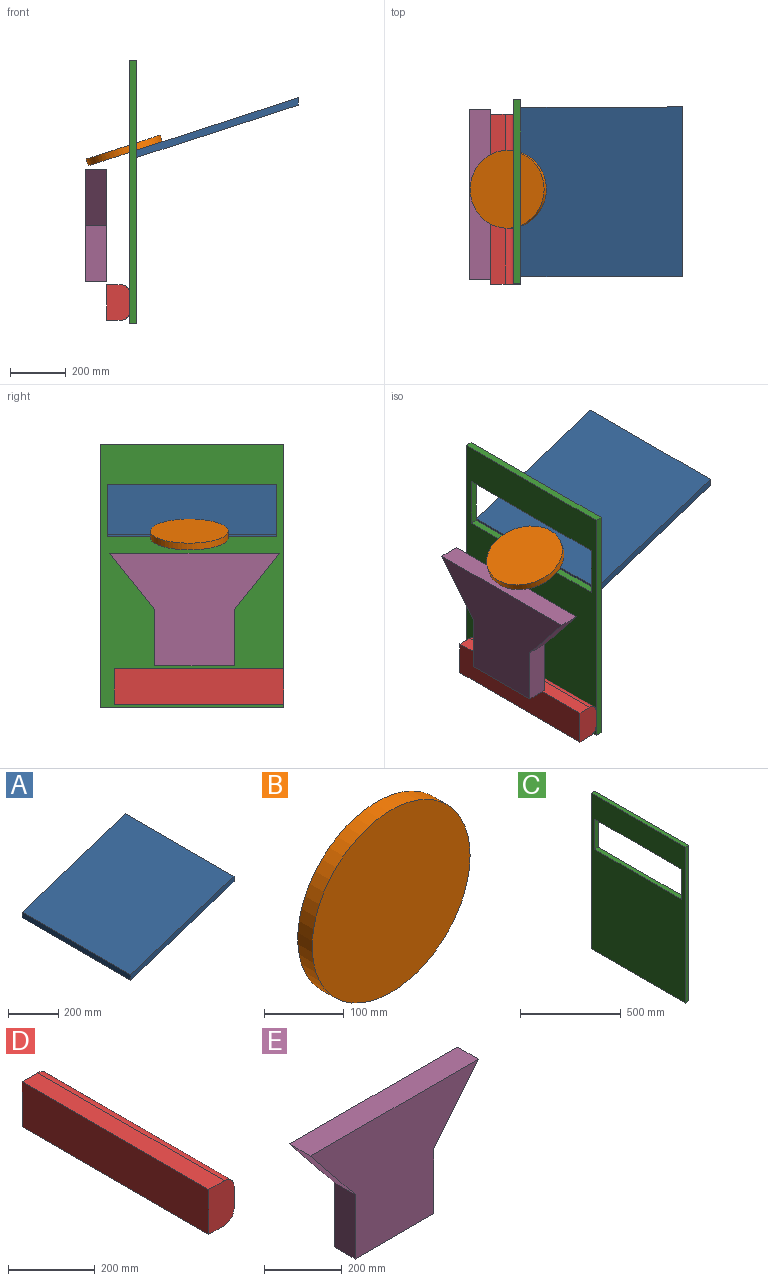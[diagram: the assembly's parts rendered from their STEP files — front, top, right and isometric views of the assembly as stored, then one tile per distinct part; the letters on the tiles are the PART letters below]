
ASSEMBLY  parts=5 mates=7
PART A: 6 faces, bbox 579.8x609.6x215.1 mm
  f0: plane 609.6x26.71mm, normal (-1,0,0), area 16280.7mm2, adj f1,f3,f4,f5
  f1: plane 609.6x579.76mm, normal (0.31,0,-0.95), area 371612.2mm2, adj f0,f2,f4,f5
  f2: plane 609.6x26.71mm, normal (1,0,0), area 16280.7mm2, adj f1,f3,f4,f5
  f3: plane 609.6x579.76mm, normal (-0.31,0,0.95), area 371612.2mm2, adj f0,f2,f4,f5
  f4: plane 579.76x215.08mm, normal (0,-1,0), area 15483.8mm2, adj f0,f1,f2,f3
  f5: plane 579.76x215.08mm, normal (0,1,0), area 15483.8mm2, adj f0,f1,f2,f3
PART B: 3 faces, bbox 279.4x25.4x279.4 mm
  f0: cylinder r=139.7mm len=279.4mm, axis (0,1,0), area 22295.1mm2, adj f1,f2
  f1: plane 279.4x279.4mm, normal (0,-1,0), area 61311.6mm2, adj f0
  f2: plane 279.4x279.4mm, normal (0,1,0), area 61311.6mm2, adj f0
PART C: 10 faces, bbox 25.4x660.4x946.2 mm
  f0: plane 946.15x660.4mm, normal (1,0,0), area 512579.6mm2, adj f2,f3,f4,f5,f6,f7,f8,f9
  f1: plane 946.15x660.4mm, normal (-1,0,0), area 512579.6mm2, adj f2,f3,f4,f5,f6,f7,f8,f9
  f2: plane 660.4x25.4mm, normal (0,0,1), area 16774.2mm2, adj f0,f1,f4,f5
  f3: plane 660.4x25.4mm, normal (0,0,-1), area 16774.2mm2, adj f0,f1,f4,f5
  f4: plane 946.15x25.4mm, normal (0,-1,0), area 24032.2mm2, adj f0,f1,f2,f3
  f5: plane 946.15x25.4mm, normal (0,1,0), area 24032.2mm2, adj f0,f1,f2,f3
  f6: plane 609.6x25.4mm, normal (0,0,1), area 15483.8mm2, adj f0,f1,f7,f9
  f7: plane 184.15x25.4mm, normal (0,1,0), area 4677.4mm2, adj f0,f1,f6,f8
  f8: plane 609.6x25.4mm, normal (0,0,-1), area 15483.8mm2, adj f0,f1,f7,f9
  f9: plane 184.15x25.4mm, normal (0,-1,0), area 4677.4mm2, adj f0,f1,f6,f8
PART D: 8 faces, bbox 82.6x609.6x127 mm
  f0: plane 609.6x63.5mm, normal (1,0,0), area 38709.6mm2, adj f1,f5,f6,f7
  f1: cylinder r=31.75mm len=609.6mm, axis (0,1,0), area 30402.4mm2, adj f0,f2,f6,f7
  f2: plane 609.6x50.8mm, normal (0,0,1), area 30967.7mm2, adj f1,f3,f6,f7
  f3: plane 609.6x127mm, normal (-1,0,0), area 77419.2mm2, adj f2,f4,f6,f7
  f4: plane 609.6x50.8mm, normal (0,0,-1), area 30967.7mm2, adj f3,f5,f6,f7
  f5: cylinder r=31.75mm len=609.6mm, axis (0,1,0), area 30402.4mm2, adj f0,f4,f6,f7
  f6: plane 127x82.55mm, normal (0,-1,0), area 10051.2mm2, adj f0,f1,f2,f3,f4,f5
  f7: plane 127x82.55mm, normal (0,1,0), area 10051.2mm2, adj f0,f1,f2,f3,f4,f5
PART E: 8 faces, bbox 609.6x76.2x404.4 mm
  f0: plane 285.75x76.2mm, normal (0,0,-1), area 21774.2mm2, adj f1,f5,f6,f7
  f1: plane 203.2x76.2mm, normal (1,0,0), area 15483.8mm2, adj f0,f2,f6,f7
  f2: plane 201.23x161.93mm, normal (0.78,0,-0.63), area 19681.6mm2, adj f1,f3,f6,f7
  f3: plane 609.6x76.2mm, normal (0,0,1), area 46451.5mm2, adj f2,f4,f6,f7
  f4: plane 201.23x161.93mm, normal (-0.78,0,-0.63), area 19681.6mm2, adj f3,f5,f6,f7
  f5: plane 203.2x76.2mm, normal (-1,0,0), area 15483.8mm2, adj f0,f4,f6,f7
  f6: plane 609.6x404.43mm, normal (0,-1,0), area 148149.5mm2, adj f0,f1,f2,f3,f4,f5
  f7: plane 609.6x404.43mm, normal (0,1,0), area 148149.5mm2, adj f0,f1,f2,f3,f4,f5
PLACE A t=(947.64,-301.6,-1225.84)mm
PLACE B rot(axis=(0.98,-0.15,0.15),91.4deg) t=(843.6,-451.24,195.88)mm
PLACE C t=(496.88,-276.2,-945.53)mm
PLACE D t=(571.27,-327,-682.59)mm
PLACE E rot(axis=(0,0,-1),90deg) t=(11.32,-1383.92,-1127.53)mm
MATE planar C.f1 <-> D.f0  axis (-1,0,0) through (93.87,-606.4,-268.41)mm
MATE planar D.f6 <-> C.f4  axis (0,-1,0) through (51.12,-936.6,-613.7)mm
MATE planar D.f3 <-> E.f7  axis (-1,0,0) through (11.32,-631.8,-613.7)mm
MATE parallel C.f3 <-> D.f4  axis (0,0,-1) through (106.57,-606.4,-689.9)mm
MATE planar B.f0 <-> A.f3  axis (0.31,0,-0.95) through (77.45,-596.93,-79.76)mm
MATE planar A.f0 <-> C.f0  axis (-1,0,0) through (119.27,-606.4,-79.53)mm
MATE planar A.f4 <-> C.f7  axis (0,-1,0) through (409.15,-911.2,14.66)mm
